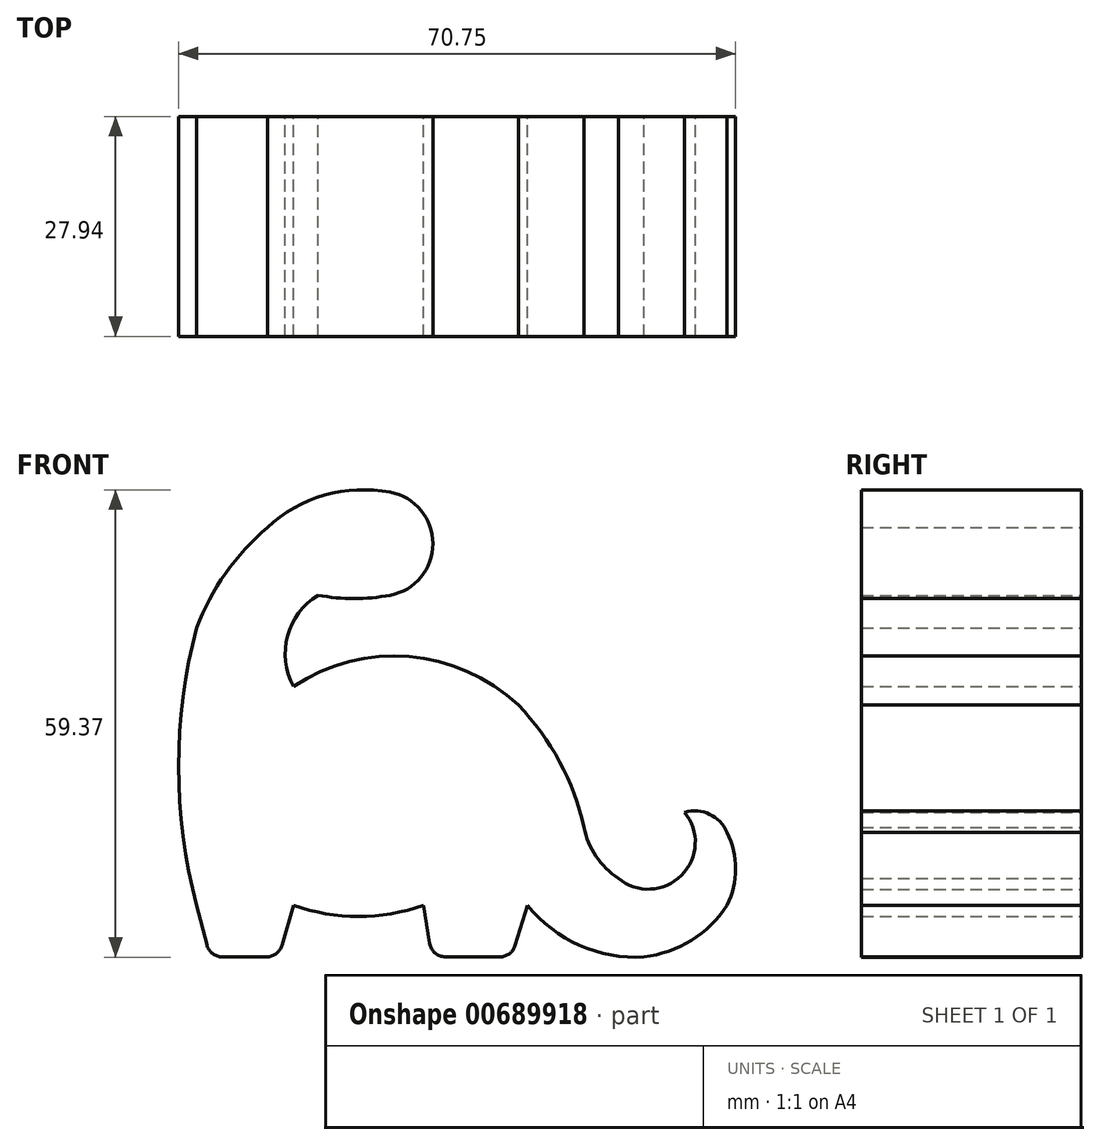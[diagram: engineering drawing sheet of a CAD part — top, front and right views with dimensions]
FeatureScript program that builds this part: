
annotation { "Feature Type Name" : "Feature", "Feature Type Description" : "" }
export const myFeature = defineFeature(function(context is Context, id is Id, definition is map)
    precondition{}
    {
        {
            var Q0;
            Q0=qCreatedBy(makeId("Front.planeOp"),FACE);
            var sketch = newSketch(context, id + "F0", { "sketchPlane" : qUnion([Q0])});
            skPoint(sketch, "E0", {"position": v(-12.3, 4.71) * mm});
            skPoint(sketch, "E1", {"position": v(28.96, -19.69) * mm});
            skPoint(sketch, "E2", {"position": v(37.37, -11.28) * mm});
            skPoint(sketch, "E3", {"position": v(32.23, -29.66) * mm});
            skPoint(sketch, "E4", {"position": v(17.44, -23.11) * mm});
            skPoint(sketch, "E5", {"position": v(4.2, -23.11) * mm});
            skPoint(sketch, "E6", {"position": v(-12.3, -23.11) * mm});
            skPoint(sketch, "E7", {"position": v(-24.6, -23.11) * mm});
            skPoint(sketch, "E8", {"position": v(0, 29.37) * mm});
            skPoint(sketch, "E9", {"position": v(0, 16.29) * mm});
            skPoint(sketch, "E10", {"position": v(-9.2, 16.29) * mm});
            skPoint(sketch, "E11", {"position": v(-22.9, -29.66) * mm});
            skPoint(sketch, "E12", {"position": v(-14.18, -29.66) * mm});
            skPoint(sketch, "E13", {"position": v(5.3, -29.66) * mm});
            skPoint(sketch, "E14", {"position": v(15.42, -29.66) * mm});
            skArc(sketch, "E15", {"start": v(28.96, -19.69) * mm, "mid": v(37, -19.3) * mm, "end": v(37.37, -11.28) * mm});
            skLineSegment(sketch, "E16", {"start": v(5.3, -29.66) * mm, "end": v(15.42, -29.66) * mm});
            skLineSegment(sketch, "E17", {"start": v(15.42, -29.66) * mm, "end": v(17.44, -23.11) * mm});
            skLineSegment(sketch, "E18", {"start": v(5.3, -29.66) * mm, "end": v(4.2, -23.11) * mm});
            skArc(sketch, "E19", {"start": v(-12.3, -23.11) * mm, "mid": v(-4.05, -24.51) * mm, "end": v(4.2, -23.11) * mm});
            skArc(sketch, "E20", {"start": v(17.44, -23.11) * mm, "mid": v(24.04, -28.18) * mm, "end": v(32.23, -29.66) * mm});
            skArc(sketch, "E21", {"start": v(32.23, -29.66) * mm, "mid": v(38.24, -27.56) * mm, "end": v(42.8, -23.11) * mm});
            skArc(sketch, "E22", {"start": v(42.8, -23.11) * mm, "mid": v(43.87, -18.49) * mm, "end": v(42.8, -13.86) * mm});
            skArc(sketch, "E23", {"start": v(0, 16.29) * mm, "mid": v(5.42, 22.83) * mm, "end": v(0, 29.37) * mm});
            skArc(sketch, "E24", {"start": v(42.8, -13.86) * mm, "mid": v(40.58, -11.53) * mm, "end": v(37.37, -11.28) * mm});
            skLineSegment(sketch, "E25", {"start": v(-12.3, -23.11) * mm, "end": v(-14.18, -29.66) * mm});
            skLineSegment(sketch, "E26", {"start": v(-14.18, -29.66) * mm, "end": v(-22.9, -29.66) * mm});
            skLineSegment(sketch, "E27", {"start": v(-24.6, -23.11) * mm, "end": v(-22.9, -29.66) * mm});
            skArc(sketch, "E28", {"start": v(0, 29.37) * mm, "mid": v(-8.34, 28.99) * mm, "end": v(-15.62, 24.9) * mm});
            skArc(sketch, "E29", {"start": v(0, 16.29) * mm, "mid": v(-4.6, 15.86) * mm, "end": v(-9.2, 16.29) * mm});
            skArc(sketch, "E30", {"start": v(-24.6, -23.11) * mm, "mid": v(-26.88, -5.49) * mm, "end": v(-24.6, 12.14) * mm});
            skArc(sketch, "E31", {"start": v(-9.2, 16.29) * mm, "mid": v(-13.03, 11.11) * mm, "end": v(-12.3, 4.71) * mm});
            skArc(sketch, "E32", {"start": v(-15.62, 24.9) * mm, "mid": v(-20.9, 19.08) * mm, "end": v(-24.6, 12.14) * mm});
            skArc(sketch, "E33", {"start": v(16.26, 2.32) * mm, "mid": v(2.4, 8.5) * mm, "end": v(-12.3, 4.71) * mm});
            skArc(sketch, "E34", {"start": v(24.62, -13.2) * mm, "mid": v(26.13, -16.89) * mm, "end": v(28.96, -19.69) * mm});
            skArc(sketch, "E35", {"start": v(24.62, -13.2) * mm, "mid": v(21.5, -4.87) * mm, "end": v(16.26, 2.32) * mm});
            skSolve(sketch);
        }
        {
            var Q0;
            Q0=makeQuery(id+"F0.imprint","IMPRINT",FACE,{"disambiguationData":[TD([[makeQuery(id+"F0.imprint","IMPRINT",EDGE,{"derivedFrom":sQuery(id+"F0.wireOp",EDGE,"E15")}),-1.0]])]});
            extrude(context, id + "F1", {"entities" : qUnion([Q0]), "depth" : 27.94 * mm, "offsetDistance" : 25.4 * mm});
        }
        {
            var Q0;
            Q0=makeQuery(id+"F1.opExtrude","SWEPT_EDGE",EDGE,{"disambiguationData":[OSD([sQuery(id+"F0.wireOp",EDGE,"E16"),sQuery(id+"F0.wireOp",EDGE,"E17")])]});
            var Q1;
            Q1=makeQuery(id+"F1.opExtrude","SWEPT_EDGE",EDGE,{"disambiguationData":[OSD([sQuery(id+"F0.wireOp",EDGE,"E16"),sQuery(id+"F0.wireOp",EDGE,"E18")])]});
            var Q2;
            Q2=makeQuery(id+"F1.opExtrude","SWEPT_EDGE",EDGE,{"disambiguationData":[OSD([sQuery(id+"F0.wireOp",EDGE,"E25"),sQuery(id+"F0.wireOp",EDGE,"E26")])]});
            var Q3;
            Q3=makeQuery(id+"F1.opExtrude","SWEPT_EDGE",EDGE,{"disambiguationData":[OSD([sQuery(id+"F0.wireOp",EDGE,"E26"),sQuery(id+"F0.wireOp",EDGE,"E27")])]});
            fillet(context, id + "F2", {"entities" : qUnion([Q0, Q1, Q2, Q3]), "radius" : 2.03 * mm, "tangentPropagation" : true, "allowEdgeOverflow" : false});
        }
    });
